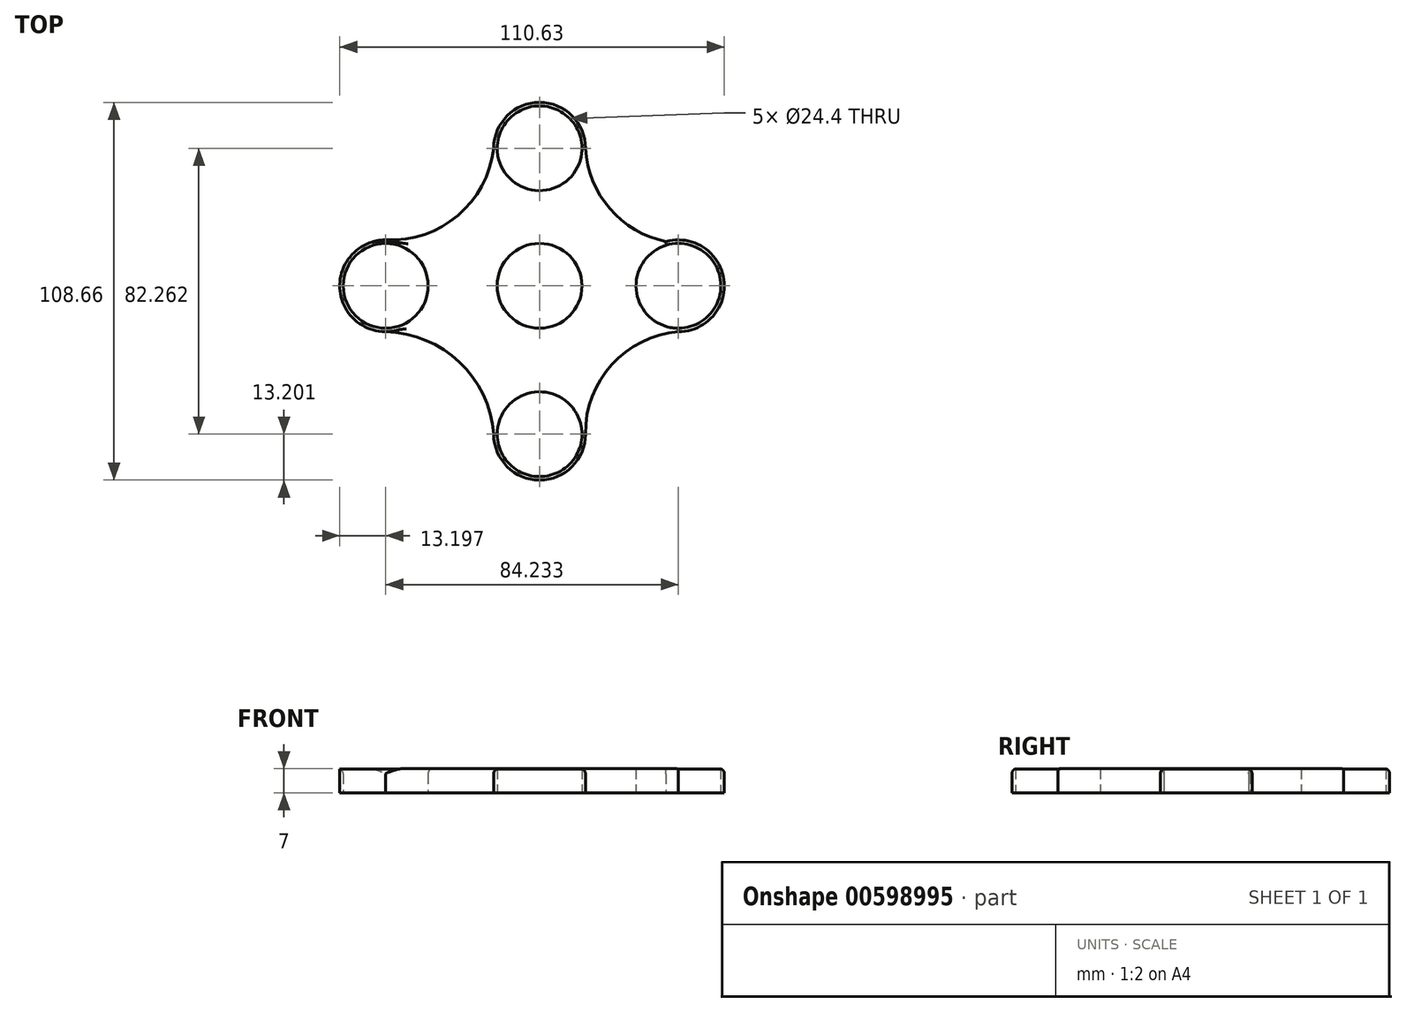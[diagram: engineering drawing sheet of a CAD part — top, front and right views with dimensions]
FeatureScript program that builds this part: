
annotation { "Feature Type Name" : "Feature", "Feature Type Description" : "" }
export const myFeature = defineFeature(function(context is Context, id is Id, definition is map)
    precondition{}
    {
        {
            var Q0;
            Q0=qCreatedBy(makeId("Top.planeOp"),FACE);
            var sketch = newSketch(context, id + "F0", { "sketchPlane" : qUnion([Q0])});
            skCircle(sketch, "E0", {"center": v(0, 0) * mm, "radius": 12.2 * mm});
            skCircle(sketch, "E1", {"center": v(0, 39.56) * mm, "radius": 12.2 * mm});
            skArc(sketch, "E2", {"start": v(13.2, 39.56) * mm, "mid": v(0, 52.76) * mm, "end": v(-13.2, 39.56) * mm});
            skCircle(sketch, "E3", {"center": v(0, -42.7) * mm, "radius": 12.2 * mm});
            skArc(sketch, "E4", {"start": v(-13.2, -42.7) * mm, "mid": v(0.11, -55.9) * mm, "end": v(13.2, -42.48) * mm});
            skCircle(sketch, "E5", {"center": v(-44.28, 0) * mm, "radius": 12.2 * mm});
            skArc(sketch, "E6", {"start": v(-43.36, 13.17) * mm, "mid": v(-57.47, 0.46) * mm, "end": v(-44.28, -13.2) * mm});
            skCircle(sketch, "E7", {"center": v(39.95, 0) * mm, "radius": 12.2 * mm});
            skArc(sketch, "E8", {"start": v(39.95, -13.2) * mm, "mid": v(53.03, 1.8) * mm, "end": v(36.39, 12.7) * mm});
            skPoint(sketch, "E9.0.midPoint", {"position": v(24.75, -20.71) * mm});
            skArc(sketch, "E10", {"start": v(-44.28, 13.2) * mm, "mid": v(-23.52, 20.23) * mm, "end": v(-13.2, 39.56) * mm});
            skArc(sketch, "E11", {"start": v(13.2, 39.56) * mm, "mid": v(21.45, 20.87) * mm, "end": v(39.95, 12.2) * mm});
            skArc(sketch, "E12", {"start": v(39.95, -13.2) * mm, "mid": v(20.78, -22.7) * mm, "end": v(13.2, -42.7) * mm});
            skArc(sketch, "E13", {"start": v(-13.2, -42.7) * mm, "mid": v(-23.06, -21.96) * mm, "end": v(-44.28, -13.2) * mm});
            skSolve(sketch);
        }
        {
            var Q0;
            Q0=makeQuery(id+"F0.imprint","IMPRINT",FACE,{"disambiguationData":[TD([[makeQuery(id+"F0.imprint","IMPRINT",EDGE,{"derivedFrom":sQuery(id+"F0.wireOp",EDGE,"E0")}),-1.0]])]});
            extrude(context, id + "F1", {"entities" : qUnion([Q0]), "depth" : 7 * mm, "offsetDistance" : 25 * mm});
        }
        {
            var Q0;
            Q0=makeQuery(id+"F1.opExtrude","CAP_EDGE",EDGE,{"disambiguationData":[OSD([sQuery(id+"F0.wireOp",EDGE,"E13")])],"isStart":false});
            var Q1;
            Q1=makeQuery(id+"F1.opExtrude","CAP_EDGE",EDGE,{"disambiguationData":[OSD([sQuery(id+"F0.wireOp",EDGE,"E10")])],"isStart":false});
            var Q2;
            Q2=makeQuery(id+"F1.opExtrude","CAP_EDGE",EDGE,{"disambiguationData":[OSD([sQuery(id+"F0.wireOp",EDGE,"E5")])],"isStart":false});
            var Q3;
            Q3=makeQuery(id+"F1.opExtrude","CAP_EDGE",EDGE,{"disambiguationData":[OSD([sQuery(id+"F0.wireOp",EDGE,"E2")])],"isStart":false});
            var Q4;
            Q4=makeQuery(id+"F1.opExtrude","CAP_EDGE",EDGE,{"disambiguationData":[OSD([sQuery(id+"F0.wireOp",EDGE,"E11")])],"isStart":false});
            var Q5;
            Q5=makeQuery(id+"F1.opExtrude","CAP_EDGE",EDGE,{"disambiguationData":[OSD([sQuery(id+"F0.wireOp",EDGE,"E8")])],"isStart":false});
            var Q6;
            Q6=makeQuery(id+"F1.opExtrude","CAP_EDGE",EDGE,{"disambiguationData":[OSD([sQuery(id+"F0.wireOp",EDGE,"E12")])],"isStart":false});
            var Q7;
            Q7=makeQuery(id+"F1.opExtrude","CAP_EDGE",EDGE,{"disambiguationData":[OSD([sQuery(id+"F0.wireOp",EDGE,"E4")])],"isStart":false});
            fillet(context, id + "F2", {"entities" : qUnion([Q0, Q1, Q2, Q3, Q4, Q5, Q6, Q7]), "radius" : 1.5 * mm, "tangentPropagation" : true, "allowEdgeOverflow" : false});
        }
    });
